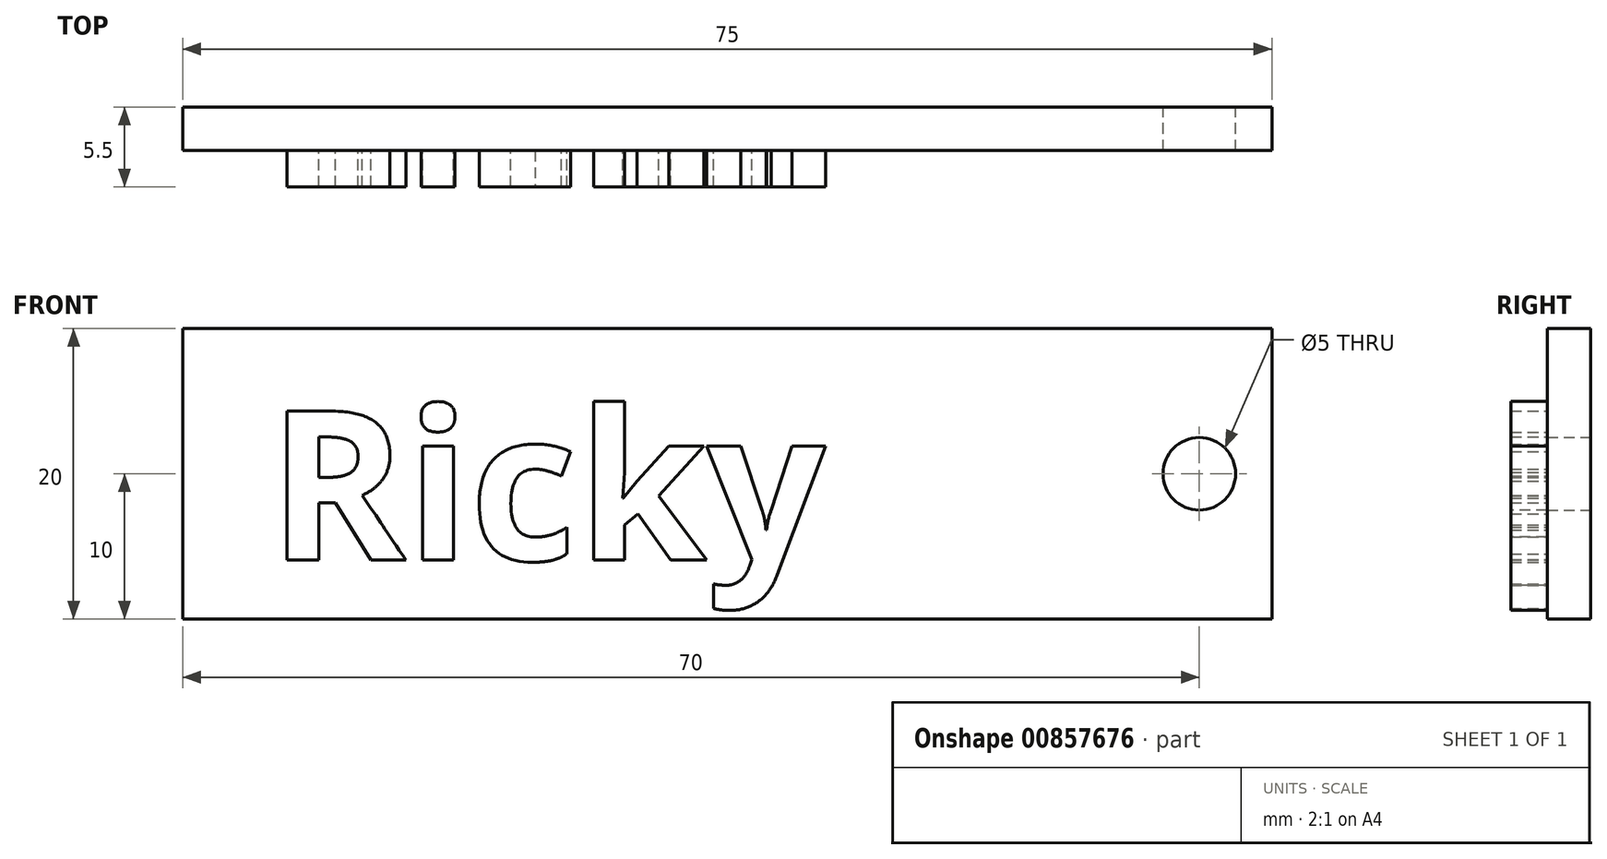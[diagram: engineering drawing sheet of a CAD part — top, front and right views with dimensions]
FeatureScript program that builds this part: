
annotation { "Feature Type Name" : "Feature", "Feature Type Description" : "" }
export const myFeature = defineFeature(function(context is Context, id is Id, definition is map)
    precondition{}
    {
        {
            var Q0;
            Q0=qCreatedBy(makeId("Front.planeOp"),FACE);
            var sketch = newSketch(context, id + "F0", { "sketchPlane" : qUnion([Q0])});
            skLineSegment(sketch, "E0.bottom", {"start": v(0, 0) * mm, "end": v(75, 0) * mm});
            skLineSegment(sketch, "E0.top", {"start": v(0, -20) * mm, "end": v(75, -20) * mm});
            skLineSegment(sketch, "E0.left", {"start": v(0, 0) * mm, "end": v(0, -20) * mm});
            skLineSegment(sketch, "E0.right", {"start": v(75, 0) * mm, "end": v(75, -20) * mm});
            skCircle(sketch, "E1", {"center": v(70, -10) * mm, "radius": 2.5 * mm});
            skSolve(sketch);
        }
        {
            var Q0;
            Q0=makeQuery(id+"F0.imprint","IMPRINT",FACE,{"disambiguationData":[TD([[makeQuery(id+"F0.imprint","IMPRINT",EDGE,{"derivedFrom":sQuery(id+"F0.wireOp",EDGE,"E0.bottom")}),-1.0]])]});
            extrude(context, id + "F1", {"entities" : qUnion([Q0]), "depth" : 3 * mm, "offsetDistance" : 25 * mm});
        }
        {
            var Q0;
            Q0=makeQuery(id+"F1.opExtrude","CAP_FACE",FACE,{"disambiguationData":[OSD([sQuery(id+"F0.wireOp",EDGE,"E0.bottom"),sQuery(id+"F0.wireOp",EDGE,"E0.top"),sQuery(id+"F0.wireOp",EDGE,"E0.left"),sQuery(id+"F0.wireOp",EDGE,"E0.right")])],"isStart":false});
            var sketch = newSketch(context, id + "F2", { "sketchPlane" : qUnion([Q0])});
            skText(sketch, "E2", { "text": "Ricky", "fontName": "OpenSans-Bold.ttf"});
            const initialGuessF2  = {"E2": [0.0059, -0.01595, 1, 0, 0.01035]};
            skSetInitialGuess(sketch, initialGuessF2);
            skSolve(sketch);
        }
        {
            var Q0;
            Q0 = qSketchRegion(id + "F2", true);
            extrude(context, id + "F3", {"entities" : qUnion([Q0]), "operationType" : NewBodyOperationType.ADD, "depth" : 2.5 * mm, "offsetDistance" : 25 * mm});
        }
    });
